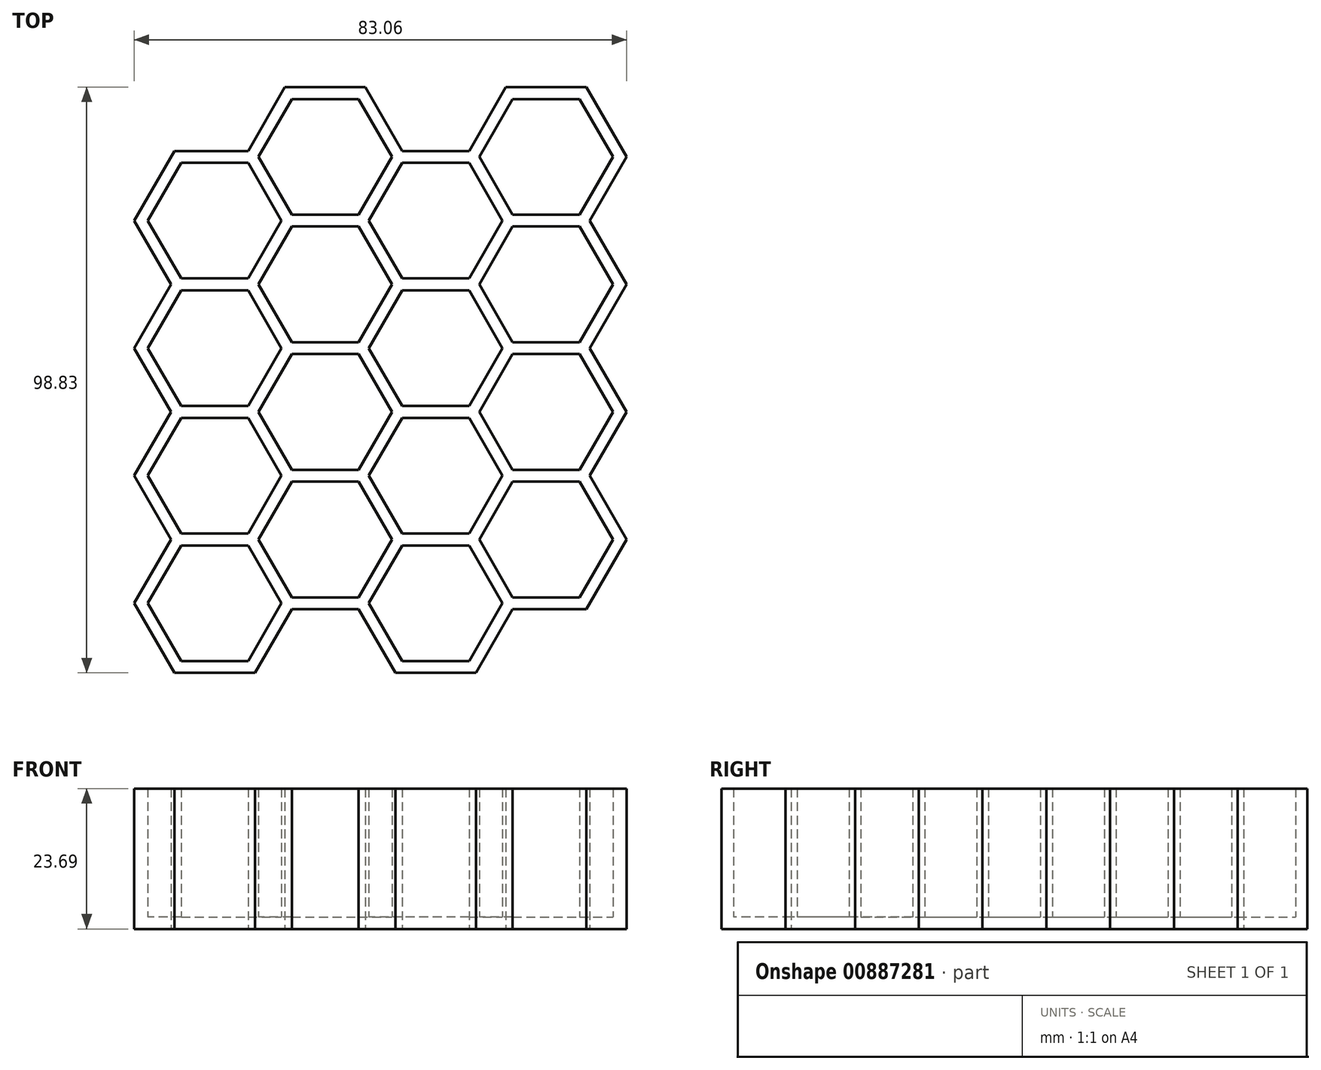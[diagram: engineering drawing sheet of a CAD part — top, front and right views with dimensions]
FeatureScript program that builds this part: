
annotation { "Feature Type Name" : "Feature", "Feature Type Description" : "" }
export const myFeature = defineFeature(function(context is Context, id is Id, definition is map)
    precondition{}
    {
        {
            var Q0;
            Q0=qCreatedBy(makeId("Top.planeOp"),FACE);
            var sketch = newSketch(context, id + "F0", { "sketchPlane" : qUnion([Q0])});
            skCircle(sketch, "E0.cCircle", {"center": v(0, 0) * mm, "radius": 9.76 * mm, "construction": true});
            skLineSegment(sketch, "E0.0", {"start": v(5.63, 9.76) * mm, "end": v(11.27, 0) * mm});
            skLineSegment(sketch, "E0.1", {"start": v(11.27, 0) * mm, "end": v(5.63, -9.76) * mm});
            skLineSegment(sketch, "E0.2", {"start": v(5.63, -9.76) * mm, "end": v(-5.63, -9.76) * mm});
            skLineSegment(sketch, "E0.3", {"start": v(-5.63, -9.76) * mm, "end": v(-11.27, 0) * mm});
            skLineSegment(sketch, "E0.4", {"start": v(-11.27, 0) * mm, "end": v(-5.63, 9.76) * mm});
            skLineSegment(sketch, "E0.5", {"start": v(-5.63, 9.76) * mm, "end": v(5.63, 9.76) * mm});
            skPoint(sketch, "E0.0.midPoint", {"position": v(8.45, 4.88) * mm});
            skPoint(sketch, "E1.0.1.0", {"position": v(8.45, 26.4) * mm});
            skLineSegment(sketch, "E1.0.1.1", {"start": v(5.63, 11.76) * mm, "end": v(-5.63, 11.76) * mm});
            skLineSegment(sketch, "E1.0.1.2", {"start": v(-5.63, 31.27) * mm, "end": v(5.63, 31.27) * mm});
            skCircle(sketch, "E1.0.1.3", {"center": v(0, 21.52) * mm, "radius": 9.76 * mm, "construction": true});
            skLineSegment(sketch, "E1.0.1.4", {"start": v(-5.63, 11.76) * mm, "end": v(-11.27, 21.52) * mm});
            skLineSegment(sketch, "E1.0.1.5", {"start": v(-11.27, 21.52) * mm, "end": v(-5.63, 31.27) * mm});
            skLineSegment(sketch, "E1.0.1.6", {"start": v(5.63, 31.27) * mm, "end": v(11.27, 21.52) * mm});
            skLineSegment(sketch, "E1.0.1.7", {"start": v(11.27, 21.52) * mm, "end": v(5.63, 11.76) * mm});
            skPoint(sketch, "E1.0.2.0", {"position": v(8.45, 47.91) * mm});
            skLineSegment(sketch, "E1.0.2.1", {"start": v(5.63, 33.27) * mm, "end": v(-5.63, 33.27) * mm});
            skLineSegment(sketch, "E1.0.2.2", {"start": v(-5.63, 52.8) * mm, "end": v(5.63, 52.8) * mm});
            skCircle(sketch, "E1.0.2.3", {"center": v(0, 43.03) * mm, "radius": 9.76 * mm, "construction": true});
            skLineSegment(sketch, "E1.0.2.4", {"start": v(-5.63, 33.27) * mm, "end": v(-11.27, 43.03) * mm});
            skLineSegment(sketch, "E1.0.2.5", {"start": v(-11.27, 43.03) * mm, "end": v(-5.63, 52.8) * mm});
            skLineSegment(sketch, "E1.0.2.6", {"start": v(5.63, 52.8) * mm, "end": v(11.27, 43.03) * mm});
            skLineSegment(sketch, "E1.0.2.7", {"start": v(11.27, 43.03) * mm, "end": v(5.63, 33.27) * mm});
            skPoint(sketch, "E1.0.3.0", {"position": v(8.45, 69.43) * mm});
            skLineSegment(sketch, "E1.0.3.1", {"start": v(5.63, 54.8) * mm, "end": v(-5.63, 54.8) * mm});
            skLineSegment(sketch, "E1.0.3.2", {"start": v(-5.63, 74.3) * mm, "end": v(5.63, 74.3) * mm});
            skCircle(sketch, "E1.0.3.3", {"center": v(0, 64.55) * mm, "radius": 9.76 * mm, "construction": true});
            skLineSegment(sketch, "E1.0.3.4", {"start": v(-5.63, 54.8) * mm, "end": v(-11.27, 64.55) * mm});
            skLineSegment(sketch, "E1.0.3.5", {"start": v(-11.27, 64.55) * mm, "end": v(-5.63, 74.3) * mm});
            skLineSegment(sketch, "E1.0.3.6", {"start": v(5.63, 74.3) * mm, "end": v(11.27, 64.55) * mm});
            skLineSegment(sketch, "E1.0.3.7", {"start": v(11.27, 64.55) * mm, "end": v(5.63, 54.8) * mm});
            skLineSegment(sketch, "E1.direction1", {"start": v(-5.63, -9.76) * mm, "end": v(27.15, -9.76) * mm, "construction": true});
            skLineSegment(sketch, "E1.direction2", {"start": v(-5.63, -9.76) * mm, "end": v(-5.63, 11.76) * mm, "construction": true});
            skCircle(sketch, "E2.cCircle", {"center": v(18.63, 10.76) * mm, "radius": 9.76 * mm, "construction": true});
            skLineSegment(sketch, "E2.0", {"start": v(24.27, 20.52) * mm, "end": v(29.9, 10.76) * mm});
            skLineSegment(sketch, "E2.1", {"start": v(29.9, 10.76) * mm, "end": v(24.27, 1) * mm});
            skLineSegment(sketch, "E2.2", {"start": v(24.27, 1) * mm, "end": v(13, 1) * mm});
            skLineSegment(sketch, "E2.3", {"start": v(13, 1) * mm, "end": v(7.37, 10.76) * mm});
            skLineSegment(sketch, "E2.4", {"start": v(7.37, 10.76) * mm, "end": v(13, 20.52) * mm});
            skLineSegment(sketch, "E2.5", {"start": v(13, 20.52) * mm, "end": v(24.27, 20.52) * mm});
            skPoint(sketch, "E2.0.midPoint", {"position": v(27.08, 15.64) * mm});
            skLineSegment(sketch, "E3.direction1", {"start": v(13, 1) * mm, "end": v(89.43, 1) * mm, "construction": true});
            skLineSegment(sketch, "E3.direction2", {"start": v(13, 1) * mm, "end": v(13, 26.4) * mm, "construction": true});
            skCircle(sketch, "E4.0.1.0", {"center": v(18.63, 32.27) * mm, "radius": 9.76 * mm, "construction": true});
            skPoint(sketch, "E4.0.1.1", {"position": v(27.08, 37.15) * mm});
            skLineSegment(sketch, "E4.0.1.2", {"start": v(13, 22.52) * mm, "end": v(89.43, 22.52) * mm, "construction": true});
            skLineSegment(sketch, "E4.0.1.3", {"start": v(13, 22.52) * mm, "end": v(7.37, 32.27) * mm});
            skLineSegment(sketch, "E4.0.1.4", {"start": v(13, 22.52) * mm, "end": v(13, 47.92) * mm, "construction": true});
            skLineSegment(sketch, "E4.0.1.5", {"start": v(29.9, 32.27) * mm, "end": v(24.27, 22.52) * mm});
            skLineSegment(sketch, "E4.0.1.6", {"start": v(13, 42.03) * mm, "end": v(24.27, 42.03) * mm});
            skLineSegment(sketch, "E4.0.1.7", {"start": v(7.37, 32.27) * mm, "end": v(13, 42.03) * mm});
            skLineSegment(sketch, "E4.0.1.8", {"start": v(24.27, 22.52) * mm, "end": v(13, 22.52) * mm});
            skLineSegment(sketch, "E4.0.1.9", {"start": v(24.27, 42.03) * mm, "end": v(29.9, 32.27) * mm});
            skCircle(sketch, "E4.0.2.0", {"center": v(18.63, 53.8) * mm, "radius": 9.76 * mm, "construction": true});
            skPoint(sketch, "E4.0.2.1", {"position": v(27.08, 58.67) * mm});
            skLineSegment(sketch, "E4.0.2.2", {"start": v(13, 44.03) * mm, "end": v(89.43, 44.03) * mm, "construction": true});
            skLineSegment(sketch, "E4.0.2.3", {"start": v(13, 44.03) * mm, "end": v(7.37, 53.8) * mm});
            skLineSegment(sketch, "E4.0.2.4", {"start": v(13, 44.03) * mm, "end": v(13, 69.43) * mm, "construction": true});
            skLineSegment(sketch, "E4.0.2.5", {"start": v(29.9, 53.8) * mm, "end": v(24.27, 44.03) * mm});
            skLineSegment(sketch, "E4.0.2.6", {"start": v(13, 63.55) * mm, "end": v(24.27, 63.55) * mm});
            skLineSegment(sketch, "E4.0.2.7", {"start": v(7.37, 53.8) * mm, "end": v(13, 63.55) * mm});
            skLineSegment(sketch, "E4.0.2.8", {"start": v(24.27, 44.03) * mm, "end": v(13, 44.03) * mm});
            skLineSegment(sketch, "E4.0.2.9", {"start": v(24.27, 63.55) * mm, "end": v(29.9, 53.8) * mm});
            skCircle(sketch, "E4.0.3.0", {"center": v(18.63, 75.3) * mm, "radius": 9.76 * mm, "construction": true});
            skPoint(sketch, "E4.0.3.1", {"position": v(27.08, 80.19) * mm});
            skLineSegment(sketch, "E4.0.3.2", {"start": v(13, 65.55) * mm, "end": v(89.43, 65.55) * mm, "construction": true});
            skLineSegment(sketch, "E4.0.3.3", {"start": v(13, 65.55) * mm, "end": v(7.37, 75.3) * mm});
            skLineSegment(sketch, "E4.0.3.4", {"start": v(13, 65.55) * mm, "end": v(13, 90.95) * mm, "construction": true});
            skLineSegment(sketch, "E4.0.3.5", {"start": v(29.9, 75.3) * mm, "end": v(24.27, 65.55) * mm});
            skLineSegment(sketch, "E4.0.3.6", {"start": v(13, 85.07) * mm, "end": v(24.27, 85.07) * mm});
            skLineSegment(sketch, "E4.0.3.7", {"start": v(7.37, 75.3) * mm, "end": v(13, 85.07) * mm});
            skLineSegment(sketch, "E4.0.3.8", {"start": v(24.27, 65.55) * mm, "end": v(13, 65.55) * mm});
            skLineSegment(sketch, "E4.0.3.9", {"start": v(24.27, 85.07) * mm, "end": v(29.9, 75.3) * mm});
            skLineSegment(sketch, "E4.direction1", {"start": v(13, 1) * mm, "end": v(50.9, 1) * mm, "construction": true});
            skLineSegment(sketch, "E4.direction2", {"start": v(13, 1) * mm, "end": v(13, 22.52) * mm, "construction": true});
            skLineSegment(sketch, "E5.1.0.0", {"start": v(31.63, -9.76) * mm, "end": v(31.63, 11.76) * mm, "construction": true});
            skLineSegment(sketch, "E5.1.0.1", {"start": v(31.63, 31.27) * mm, "end": v(42.9, 31.27) * mm});
            skPoint(sketch, "E5.1.0.2", {"position": v(45.72, 69.43) * mm});
            skLineSegment(sketch, "E5.1.0.3", {"start": v(31.63, 52.8) * mm, "end": v(42.9, 52.8) * mm});
            skPoint(sketch, "E5.1.0.4", {"position": v(45.72, 47.91) * mm});
            skPoint(sketch, "E5.1.0.5", {"position": v(45.72, 26.4) * mm});
            skCircle(sketch, "E5.1.0.6", {"center": v(37.27, 21.52) * mm, "radius": 9.76 * mm, "construction": true});
            skCircle(sketch, "E5.1.0.7", {"center": v(37.27, 0) * mm, "radius": 9.76 * mm, "construction": true});
            skCircle(sketch, "E5.1.0.8", {"center": v(37.27, 64.55) * mm, "radius": 9.76 * mm, "construction": true});
            skLineSegment(sketch, "E5.1.0.9", {"start": v(42.9, 11.76) * mm, "end": v(31.63, 11.76) * mm});
            skCircle(sketch, "E5.1.0.10", {"center": v(37.27, 43.03) * mm, "radius": 9.76 * mm, "construction": true});
            skPoint(sketch, "E5.1.0.11", {"position": v(45.72, 4.88) * mm});
            skLineSegment(sketch, "E5.1.0.12", {"start": v(42.9, -9.76) * mm, "end": v(31.63, -9.76) * mm});
            skLineSegment(sketch, "E5.1.0.13", {"start": v(42.9, 33.27) * mm, "end": v(31.63, 33.27) * mm});
            skLineSegment(sketch, "E5.1.0.14", {"start": v(26, 64.55) * mm, "end": v(31.63, 74.3) * mm});
            skLineSegment(sketch, "E5.1.0.15", {"start": v(42.9, 74.3) * mm, "end": v(48.54, 64.55) * mm});
            skLineSegment(sketch, "E5.1.0.16", {"start": v(48.54, 0) * mm, "end": v(42.9, -9.76) * mm});
            skLineSegment(sketch, "E5.1.0.17", {"start": v(42.9, 9.76) * mm, "end": v(48.54, 0) * mm});
            skLineSegment(sketch, "E5.1.0.18", {"start": v(42.9, 54.8) * mm, "end": v(31.63, 54.8) * mm});
            skLineSegment(sketch, "E5.1.0.19", {"start": v(31.63, 74.3) * mm, "end": v(42.9, 74.3) * mm});
            skLineSegment(sketch, "E5.1.0.20", {"start": v(31.63, 11.76) * mm, "end": v(26, 21.52) * mm});
            skLineSegment(sketch, "E5.1.0.21", {"start": v(42.9, 31.27) * mm, "end": v(48.54, 21.52) * mm});
            skLineSegment(sketch, "E5.1.0.22", {"start": v(48.54, 21.52) * mm, "end": v(42.9, 11.76) * mm});
            skLineSegment(sketch, "E5.1.0.23", {"start": v(26, 0) * mm, "end": v(31.63, 9.76) * mm});
            skLineSegment(sketch, "E5.1.0.24", {"start": v(31.63, 9.76) * mm, "end": v(42.9, 9.76) * mm});
            skLineSegment(sketch, "E5.1.0.25", {"start": v(31.63, -9.76) * mm, "end": v(26, 0) * mm});
            skLineSegment(sketch, "E5.1.0.26", {"start": v(48.54, 64.55) * mm, "end": v(42.9, 54.8) * mm});
            skLineSegment(sketch, "E5.1.0.27", {"start": v(48.54, 43.03) * mm, "end": v(42.9, 33.27) * mm});
            skLineSegment(sketch, "E5.1.0.28", {"start": v(26, 21.52) * mm, "end": v(31.63, 31.27) * mm});
            skLineSegment(sketch, "E5.1.0.29", {"start": v(26, 43.03) * mm, "end": v(31.63, 52.8) * mm});
            skLineSegment(sketch, "E5.1.0.30", {"start": v(42.9, 52.8) * mm, "end": v(48.54, 43.03) * mm});
            skLineSegment(sketch, "E5.1.0.31", {"start": v(31.63, 54.8) * mm, "end": v(26, 64.55) * mm});
            skLineSegment(sketch, "E5.1.0.32", {"start": v(31.63, 33.27) * mm, "end": v(26, 43.03) * mm});
            skLineSegment(sketch, "E5.direction1", {"start": v(-5.63, -9.76) * mm, "end": v(31.63, -9.76) * mm, "construction": true});
            skLineSegment(sketch, "E6.0", {"start": v(25.42, 87.07) * mm, "end": v(31.63, 76.3) * mm});
            skLineSegment(sketch, "E6.1", {"start": v(11.85, 87.07) * mm, "end": v(25.42, 87.07) * mm});
            skLineSegment(sketch, "E7.0", {"start": v(-6.79, 76.3) * mm, "end": v(5.63, 76.3) * mm});
            skLineSegment(sketch, "E7.1", {"start": v(-13.58, 64.55) * mm, "end": v(-6.79, 76.3) * mm});
            skLineSegment(sketch, "E7.2", {"start": v(-7.37, 53.8) * mm, "end": v(-13.58, 64.55) * mm});
            skLineSegment(sketch, "E8.0", {"start": v(-13.58, 43.03) * mm, "end": v(-7.37, 53.8) * mm});
            skLineSegment(sketch, "E9.0", {"start": v(-13.58, 21.52) * mm, "end": v(-7.37, 32.27) * mm});
            skLineSegment(sketch, "E9.1", {"start": v(-7.37, 10.76) * mm, "end": v(-13.58, 21.52) * mm});
            skLineSegment(sketch, "E10.0", {"start": v(-13.58, 0) * mm, "end": v(-7.37, 10.76) * mm});
            skLineSegment(sketch, "E10.1", {"start": v(-6.79, -11.76) * mm, "end": v(-13.58, 0) * mm});
            skLineSegment(sketch, "E10.2", {"start": v(6.79, -11.76) * mm, "end": v(-6.79, -11.76) * mm});
            skLineSegment(sketch, "E10.3", {"start": v(13, -1) * mm, "end": v(6.79, -11.76) * mm});
            skPoint(sketch, "E11.1.0.0", {"position": v(64.35, 80.19) * mm});
            skCircle(sketch, "E11.1.0.1", {"center": v(55.9, 32.27) * mm, "radius": 9.76 * mm, "construction": true});
            skPoint(sketch, "E11.1.0.2", {"position": v(64.35, 58.67) * mm});
            skLineSegment(sketch, "E11.1.0.3", {"start": v(50.27, 44.03) * mm, "end": v(50.27, 69.43) * mm, "construction": true});
            skLineSegment(sketch, "E11.1.0.4", {"start": v(50.27, 1) * mm, "end": v(50.27, 26.4) * mm, "construction": true});
            skLineSegment(sketch, "E11.1.0.5", {"start": v(50.27, 22.52) * mm, "end": v(50.27, 47.92) * mm, "construction": true});
            skPoint(sketch, "E11.1.0.6", {"position": v(64.35, 15.64) * mm});
            skLineSegment(sketch, "E11.1.0.8", {"start": v(50.27, 65.55) * mm, "end": v(50.27, 90.95) * mm, "construction": true});
            skCircle(sketch, "E11.1.0.9", {"center": v(55.9, 10.76) * mm, "radius": 9.76 * mm, "construction": true});
            skPoint(sketch, "E11.1.0.10", {"position": v(64.35, 37.15) * mm});
            skCircle(sketch, "E11.1.0.11", {"center": v(55.9, 53.8) * mm, "radius": 9.76 * mm, "construction": true});
            skCircle(sketch, "E11.1.0.12", {"center": v(55.9, 75.3) * mm, "radius": 9.76 * mm, "construction": true});
            skLineSegment(sketch, "E11.1.0.14", {"start": v(61.54, 22.52) * mm, "end": v(50.27, 22.52) * mm});
            skLineSegment(sketch, "E11.1.0.15", {"start": v(61.54, 42.03) * mm, "end": v(67.17, 32.27) * mm});
            skLineSegment(sketch, "E11.1.0.16", {"start": v(61.54, 63.55) * mm, "end": v(67.17, 53.8) * mm});
            skLineSegment(sketch, "E11.1.0.17", {"start": v(50.27, 1) * mm, "end": v(44.63, 10.76) * mm});
            skLineSegment(sketch, "E11.1.0.18", {"start": v(61.54, 1) * mm, "end": v(50.27, 1) * mm});
            skLineSegment(sketch, "E11.1.0.19", {"start": v(50.27, 85.07) * mm, "end": v(61.54, 85.07) * mm});
            skLineSegment(sketch, "E11.1.0.20", {"start": v(67.17, 75.3) * mm, "end": v(61.54, 65.55) * mm});
            skLineSegment(sketch, "E11.1.0.21", {"start": v(50.27, 22.52) * mm, "end": v(44.63, 32.27) * mm});
            skLineSegment(sketch, "E11.1.0.22", {"start": v(50.27, 42.03) * mm, "end": v(61.54, 42.03) * mm});
            skLineSegment(sketch, "E11.1.0.23", {"start": v(50.27, 1) * mm, "end": v(50.27, 22.52) * mm, "construction": true});
            skLineSegment(sketch, "E11.1.0.24", {"start": v(61.54, 44.03) * mm, "end": v(50.27, 44.03) * mm});
            skLineSegment(sketch, "E11.1.0.25", {"start": v(50.27, 65.55) * mm, "end": v(44.63, 75.3) * mm});
            skLineSegment(sketch, "E11.1.0.26", {"start": v(44.63, 32.27) * mm, "end": v(50.27, 42.03) * mm});
            skLineSegment(sketch, "E11.1.0.27", {"start": v(61.54, 85.07) * mm, "end": v(67.17, 75.3) * mm});
            skLineSegment(sketch, "E11.1.0.28", {"start": v(61.54, 65.55) * mm, "end": v(50.27, 65.55) * mm});
            skLineSegment(sketch, "E11.1.0.29", {"start": v(67.17, 53.8) * mm, "end": v(61.54, 44.03) * mm});
            skLineSegment(sketch, "E11.1.0.30", {"start": v(50.27, 44.03) * mm, "end": v(44.63, 53.8) * mm});
            skLineSegment(sketch, "E11.1.0.31", {"start": v(44.63, 53.8) * mm, "end": v(50.27, 63.55) * mm});
            skLineSegment(sketch, "E11.1.0.32", {"start": v(50.27, 20.52) * mm, "end": v(61.54, 20.52) * mm});
            skLineSegment(sketch, "E11.1.0.33", {"start": v(44.63, 10.76) * mm, "end": v(50.27, 20.52) * mm});
            skLineSegment(sketch, "E11.1.0.34", {"start": v(67.17, 32.27) * mm, "end": v(61.54, 22.52) * mm});
            skLineSegment(sketch, "E11.1.0.35", {"start": v(44.63, 75.3) * mm, "end": v(50.27, 85.07) * mm});
            skLineSegment(sketch, "E11.1.0.36", {"start": v(50.27, 63.55) * mm, "end": v(61.54, 63.55) * mm});
            skLineSegment(sketch, "E11.1.0.37", {"start": v(67.17, 10.76) * mm, "end": v(61.54, 1) * mm});
            skLineSegment(sketch, "E11.1.0.38", {"start": v(61.54, 20.52) * mm, "end": v(67.17, 10.76) * mm});
            skLineSegment(sketch, "E11.direction1", {"start": v(25.5, -2.85) * mm, "end": v(64.28, -2.85) * mm, "construction": true});
            skLineSegment(sketch, "E12.0", {"start": v(31.63, 76.3) * mm, "end": v(42.9, 76.3) * mm});
            skLineSegment(sketch, "E13.0", {"start": v(69.48, 75.3) * mm, "end": v(63.27, 64.55) * mm});
            skLineSegment(sketch, "E13.1", {"start": v(62.7, 87.07) * mm, "end": v(69.48, 75.3) * mm});
            skLineSegment(sketch, "E13.2", {"start": v(49.11, 87.07) * mm, "end": v(62.7, 87.07) * mm});
            skLineSegment(sketch, "E14.0", {"start": v(69.48, 53.8) * mm, "end": v(63.27, 43.03) * mm});
            skLineSegment(sketch, "E14.1", {"start": v(63.27, 64.55) * mm, "end": v(69.48, 53.8) * mm});
            skLineSegment(sketch, "E15.0", {"start": v(69.48, 32.27) * mm, "end": v(63.27, 21.52) * mm});
            skLineSegment(sketch, "E15.1", {"start": v(63.27, 43.03) * mm, "end": v(69.48, 32.27) * mm});
            skLineSegment(sketch, "E16.0", {"start": v(62.7, -1) * mm, "end": v(50.27, -1) * mm});
            skLineSegment(sketch, "E16.1", {"start": v(69.48, 10.76) * mm, "end": v(62.7, -1) * mm});
            skLineSegment(sketch, "E16.2", {"start": v(63.27, 21.52) * mm, "end": v(69.48, 10.76) * mm});
            skLineSegment(sketch, "E17.0", {"start": v(30.48, -11.76) * mm, "end": v(24.27, -1) * mm});
            skLineSegment(sketch, "E17.1", {"start": v(44.06, -11.76) * mm, "end": v(30.48, -11.76) * mm});
            skLineSegment(sketch, "E17.2", {"start": v(50.27, -1) * mm, "end": v(44.06, -11.76) * mm});
            skLineSegment(sketch, "E18.0", {"start": v(24.27, -1) * mm, "end": v(13, -1) * mm});
            skLineSegment(sketch, "E19.trimOffspring", {"start": v(-7.37, 32.27) * mm, "end": v(-13.58, 43.03) * mm});
            skLineSegment(sketch, "E20.trimOffspring", {"start": v(42.9, 76.3) * mm, "end": v(49.11, 87.07) * mm});
            skLineSegment(sketch, "E21.trimOffspring", {"start": v(5.63, 76.3) * mm, "end": v(11.85, 87.07) * mm});
            skSolve(sketch);
        }
        {
            var Q0;
            Q0=makeQuery(id+"F0.imprint","IMPRINT",FACE,{"disambiguationData":[TD([[makeQuery(id+"F0.imprint","IMPRINT",EDGE,{"derivedFrom":sQuery(id+"F0.wireOp",EDGE,"E0.0")}),1.0]])]});
            extrude(context, id + "F1", {"entities" : qUnion([Q0]), "depth" : 21.7 * mm, "offsetDistance" : 25.4 * mm});
        }
        {
            var Q0;
            Q0=makeQuery(id+"F1.opExtrude","CAP_FACE",FACE,{"disambiguationData":[OSD([sQuery(id+"F0.wireOp",EDGE,"E0.0"),sQuery(id+"F0.wireOp",EDGE,"E0.1"),sQuery(id+"F0.wireOp",EDGE,"E0.2"),sQuery(id+"F0.wireOp",EDGE,"E0.3"),sQuery(id+"F0.wireOp",EDGE,"E0.4"),sQuery(id+"F0.wireOp",EDGE,"E0.5"),sQuery(id+"F0.wireOp",EDGE,"E1.0.1.1"),sQuery(id+"F0.wireOp",EDGE,"E1.0.1.2"),sQuery(id+"F0.wireOp",EDGE,"E1.0.1.4"),sQuery(id+"F0.wireOp",EDGE,"E1.0.1.5"),sQuery(id+"F0.wireOp",EDGE,"E1.0.1.6"),sQuery(id+"F0.wireOp",EDGE,"E1.0.1.7"),sQuery(id+"F0.wireOp",EDGE,"E1.0.2.1"),sQuery(id+"F0.wireOp",EDGE,"E1.0.2.2"),sQuery(id+"F0.wireOp",EDGE,"E1.0.2.4"),sQuery(id+"F0.wireOp",EDGE,"E1.0.2.5"),sQuery(id+"F0.wireOp",EDGE,"E1.0.2.6"),sQuery(id+"F0.wireOp",EDGE,"E1.0.2.7"),sQuery(id+"F0.wireOp",EDGE,"E1.0.3.1"),sQuery(id+"F0.wireOp",EDGE,"E1.0.3.2"),sQuery(id+"F0.wireOp",EDGE,"E1.0.3.4"),sQuery(id+"F0.wireOp",EDGE,"E1.0.3.5"),sQuery(id+"F0.wireOp",EDGE,"E1.0.3.6"),sQuery(id+"F0.wireOp",EDGE,"E1.0.3.7"),sQuery(id+"F0.wireOp",EDGE,"E2.0"),sQuery(id+"F0.wireOp",EDGE,"E2.1"),sQuery(id+"F0.wireOp",EDGE,"E2.2"),sQuery(id+"F0.wireOp",EDGE,"E2.3"),sQuery(id+"F0.wireOp",EDGE,"E2.4"),sQuery(id+"F0.wireOp",EDGE,"E2.5"),sQuery(id+"F0.wireOp",EDGE,"E4.0.1.3"),sQuery(id+"F0.wireOp",EDGE,"E4.0.1.5"),sQuery(id+"F0.wireOp",EDGE,"E4.0.1.6"),sQuery(id+"F0.wireOp",EDGE,"E4.0.1.7"),sQuery(id+"F0.wireOp",EDGE,"E4.0.1.8"),sQuery(id+"F0.wireOp",EDGE,"E4.0.1.9"),sQuery(id+"F0.wireOp",EDGE,"E4.0.2.3"),sQuery(id+"F0.wireOp",EDGE,"E4.0.2.5"),sQuery(id+"F0.wireOp",EDGE,"E4.0.2.6"),sQuery(id+"F0.wireOp",EDGE,"E4.0.2.7"),sQuery(id+"F0.wireOp",EDGE,"E4.0.2.8"),sQuery(id+"F0.wireOp",EDGE,"E4.0.2.9"),sQuery(id+"F0.wireOp",EDGE,"E4.0.3.3"),sQuery(id+"F0.wireOp",EDGE,"E4.0.3.5"),sQuery(id+"F0.wireOp",EDGE,"E4.0.3.6"),sQuery(id+"F0.wireOp",EDGE,"E4.0.3.7"),sQuery(id+"F0.wireOp",EDGE,"E4.0.3.8"),sQuery(id+"F0.wireOp",EDGE,"E4.0.3.9"),sQuery(id+"F0.wireOp",EDGE,"E5.1.0.1"),sQuery(id+"F0.wireOp",EDGE,"E5.1.0.3"),sQuery(id+"F0.wireOp",EDGE,"E5.1.0.9"),sQuery(id+"F0.wireOp",EDGE,"E5.1.0.12"),sQuery(id+"F0.wireOp",EDGE,"E5.1.0.13"),sQuery(id+"F0.wireOp",EDGE,"E5.1.0.14"),sQuery(id+"F0.wireOp",EDGE,"E5.1.0.15"),sQuery(id+"F0.wireOp",EDGE,"E5.1.0.16"),sQuery(id+"F0.wireOp",EDGE,"E5.1.0.17"),sQuery(id+"F0.wireOp",EDGE,"E5.1.0.18"),sQuery(id+"F0.wireOp",EDGE,"E5.1.0.19"),sQuery(id+"F0.wireOp",EDGE,"E5.1.0.20"),sQuery(id+"F0.wireOp",EDGE,"E5.1.0.21"),sQuery(id+"F0.wireOp",EDGE,"E5.1.0.22"),sQuery(id+"F0.wireOp",EDGE,"E5.1.0.23"),sQuery(id+"F0.wireOp",EDGE,"E5.1.0.24"),sQuery(id+"F0.wireOp",EDGE,"E5.1.0.25"),sQuery(id+"F0.wireOp",EDGE,"E5.1.0.26"),sQuery(id+"F0.wireOp",EDGE,"E5.1.0.27"),sQuery(id+"F0.wireOp",EDGE,"E5.1.0.28"),sQuery(id+"F0.wireOp",EDGE,"E5.1.0.29"),sQuery(id+"F0.wireOp",EDGE,"E5.1.0.30"),sQuery(id+"F0.wireOp",EDGE,"E5.1.0.31"),sQuery(id+"F0.wireOp",EDGE,"E5.1.0.32"),sQuery(id+"F0.wireOp",EDGE,"E6.0"),sQuery(id+"F0.wireOp",EDGE,"E6.1"),sQuery(id+"F0.wireOp",EDGE,"E6.2"),sQuery(id+"F0.wireOp",EDGE,"E7.0"),sQuery(id+"F0.wireOp",EDGE,"E7.1"),sQuery(id+"F0.wireOp",EDGE,"E7.2"),sQuery(id+"F0.wireOp",EDGE,"E8.0"),sQuery(id+"F0.wireOp",EDGE,"E8.1"),sQuery(id+"F0.wireOp",EDGE,"E9.0"),sQuery(id+"F0.wireOp",EDGE,"E9.1"),sQuery(id+"F0.wireOp",EDGE,"E10.0"),sQuery(id+"F0.wireOp",EDGE,"E10.1"),sQuery(id+"F0.wireOp",EDGE,"E10.2"),sQuery(id+"F0.wireOp",EDGE,"E10.3"),sQuery(id+"F0.wireOp",EDGE,"E11.1.0.14"),sQuery(id+"F0.wireOp",EDGE,"E11.1.0.15"),sQuery(id+"F0.wireOp",EDGE,"E11.1.0.16"),sQuery(id+"F0.wireOp",EDGE,"E11.1.0.17"),sQuery(id+"F0.wireOp",EDGE,"E11.1.0.18"),sQuery(id+"F0.wireOp",EDGE,"E11.1.0.19"),sQuery(id+"F0.wireOp",EDGE,"E11.1.0.20"),sQuery(id+"F0.wireOp",EDGE,"E11.1.0.21"),sQuery(id+"F0.wireOp",EDGE,"E11.1.0.22"),sQuery(id+"F0.wireOp",EDGE,"E11.1.0.24"),sQuery(id+"F0.wireOp",EDGE,"E11.1.0.25"),sQuery(id+"F0.wireOp",EDGE,"E11.1.0.26"),sQuery(id+"F0.wireOp",EDGE,"E11.1.0.27"),sQuery(id+"F0.wireOp",EDGE,"E11.1.0.28"),sQuery(id+"F0.wireOp",EDGE,"E11.1.0.29"),sQuery(id+"F0.wireOp",EDGE,"E11.1.0.30"),sQuery(id+"F0.wireOp",EDGE,"E11.1.0.31"),sQuery(id+"F0.wireOp",EDGE,"E11.1.0.32"),sQuery(id+"F0.wireOp",EDGE,"E11.1.0.33"),sQuery(id+"F0.wireOp",EDGE,"E11.1.0.34"),sQuery(id+"F0.wireOp",EDGE,"E11.1.0.35"),sQuery(id+"F0.wireOp",EDGE,"E11.1.0.36"),sQuery(id+"F0.wireOp",EDGE,"E11.1.0.37"),sQuery(id+"F0.wireOp",EDGE,"E11.1.0.38"),sQuery(id+"F0.wireOp",EDGE,"E12.0"),sQuery(id+"F0.wireOp",EDGE,"E13.0"),sQuery(id+"F0.wireOp",EDGE,"E13.1"),sQuery(id+"F0.wireOp",EDGE,"E13.2"),sQuery(id+"F0.wireOp",EDGE,"E13.3"),sQuery(id+"F0.wireOp",EDGE,"E14.0"),sQuery(id+"F0.wireOp",EDGE,"E14.1"),sQuery(id+"F0.wireOp",EDGE,"E15.0"),sQuery(id+"F0.wireOp",EDGE,"E15.1"),sQuery(id+"F0.wireOp",EDGE,"E16.0"),sQuery(id+"F0.wireOp",EDGE,"E16.1"),sQuery(id+"F0.wireOp",EDGE,"E16.2"),sQuery(id+"F0.wireOp",EDGE,"E17.0"),sQuery(id+"F0.wireOp",EDGE,"E17.1"),sQuery(id+"F0.wireOp",EDGE,"E17.2"),sQuery(id+"F0.wireOp",EDGE,"E18.0")])],"isStart":true});
            var sketch = newSketch(context, id + "F2", { "sketchPlane" : qUnion([Q0])});
            skLineSegment(sketch, "E22.0", {"start": v(62.7, -87.07) * mm, "end": v(69.48, -75.3) * mm});
            skLineSegment(sketch, "E23.0", {"start": v(69.48, -75.3) * mm, "end": v(63.27, -64.55) * mm});
            skLineSegment(sketch, "E24.0", {"start": v(63.27, -64.55) * mm, "end": v(69.48, -53.8) * mm});
            skLineSegment(sketch, "E25.0", {"start": v(69.48, -53.8) * mm, "end": v(63.27, -43.03) * mm});
            skLineSegment(sketch, "E26.0", {"start": v(63.27, -43.03) * mm, "end": v(69.48, -32.27) * mm});
            skLineSegment(sketch, "E27.0", {"start": v(69.48, -32.27) * mm, "end": v(63.27, -21.52) * mm});
            skLineSegment(sketch, "E28.0", {"start": v(63.27, -21.52) * mm, "end": v(69.48, -10.76) * mm});
            skLineSegment(sketch, "E29.0", {"start": v(69.48, -10.76) * mm, "end": v(62.7, 1) * mm});
            skLineSegment(sketch, "E30.0", {"start": v(62.7, 1) * mm, "end": v(50.27, 1) * mm});
            skLineSegment(sketch, "E31.0", {"start": v(50.27, 1) * mm, "end": v(44.06, 11.76) * mm});
            skLineSegment(sketch, "E32.0", {"start": v(44.06, 11.76) * mm, "end": v(30.48, 11.76) * mm});
            skLineSegment(sketch, "E33.0", {"start": v(30.48, 11.76) * mm, "end": v(24.27, 1) * mm});
            skLineSegment(sketch, "E34.0", {"start": v(24.27, 1) * mm, "end": v(13, 1) * mm});
            skLineSegment(sketch, "E35.0", {"start": v(13, 1) * mm, "end": v(6.79, 11.76) * mm});
            skLineSegment(sketch, "E36.0", {"start": v(6.79, 11.76) * mm, "end": v(-6.79, 11.76) * mm});
            skLineSegment(sketch, "E37.0", {"start": v(-6.79, 11.76) * mm, "end": v(-13.58, 0) * mm});
            skLineSegment(sketch, "E38.0", {"start": v(-13.58, 0) * mm, "end": v(-7.37, -10.76) * mm});
            skLineSegment(sketch, "E39.0", {"start": v(-7.37, -10.76) * mm, "end": v(-13.58, -21.52) * mm});
            skLineSegment(sketch, "E40.0", {"start": v(-13.58, -21.52) * mm, "end": v(-13.58, -21.52) * mm});
            skLineSegment(sketch, "E41.0", {"start": v(-7.37, -53.8) * mm, "end": v(-13.58, -64.55) * mm});
            skLineSegment(sketch, "E42.0", {"start": v(-13.58, -64.55) * mm, "end": v(-6.79, -76.3) * mm});
            skLineSegment(sketch, "E43.0", {"start": v(-6.79, -76.3) * mm, "end": v(-6.79, -76.3) * mm});
            skLineSegment(sketch, "E44.0", {"start": v(25.42, -87.07) * mm, "end": v(31.63, -76.3) * mm});
            skLineSegment(sketch, "E45.0", {"start": v(-13.58, -43.03) * mm, "end": v(-7.37, -53.8) * mm});
            skLineSegment(sketch, "E46.0", {"start": v(-7.37, -32.27) * mm, "end": v(-13.58, -43.03) * mm});
            skLineSegment(sketch, "E47.0", {"start": v(-13.58, -21.52) * mm, "end": v(-7.37, -32.27) * mm});
            skLineSegment(sketch, "E48.0", {"start": v(49.11, -87.07) * mm, "end": v(62.7, -87.07) * mm});
            skLineSegment(sketch, "E49.0", {"start": v(42.9, -76.3) * mm, "end": v(49.11, -87.07) * mm});
            skLineSegment(sketch, "E50.0", {"start": v(31.63, -76.3) * mm, "end": v(42.9, -76.3) * mm});
            skLineSegment(sketch, "E51.0", {"start": v(11.85, -87.07) * mm, "end": v(25.42, -87.07) * mm});
            skLineSegment(sketch, "E52.0", {"start": v(5.63, -76.3) * mm, "end": v(11.85, -87.07) * mm});
            skLineSegment(sketch, "E53.0", {"start": v(-6.79, -76.3) * mm, "end": v(5.63, -76.3) * mm});
            skSolve(sketch);
        }
        {
            var Q0;
            Q0 = qSketchRegion(id + "F2", true);
            extrude(context, id + "F3", {"entities" : qUnion([Q0]), "operationType" : NewBodyOperationType.ADD, "depth" : 2 * mm, "offsetDistance" : 25.4 * mm});
        }
    });
